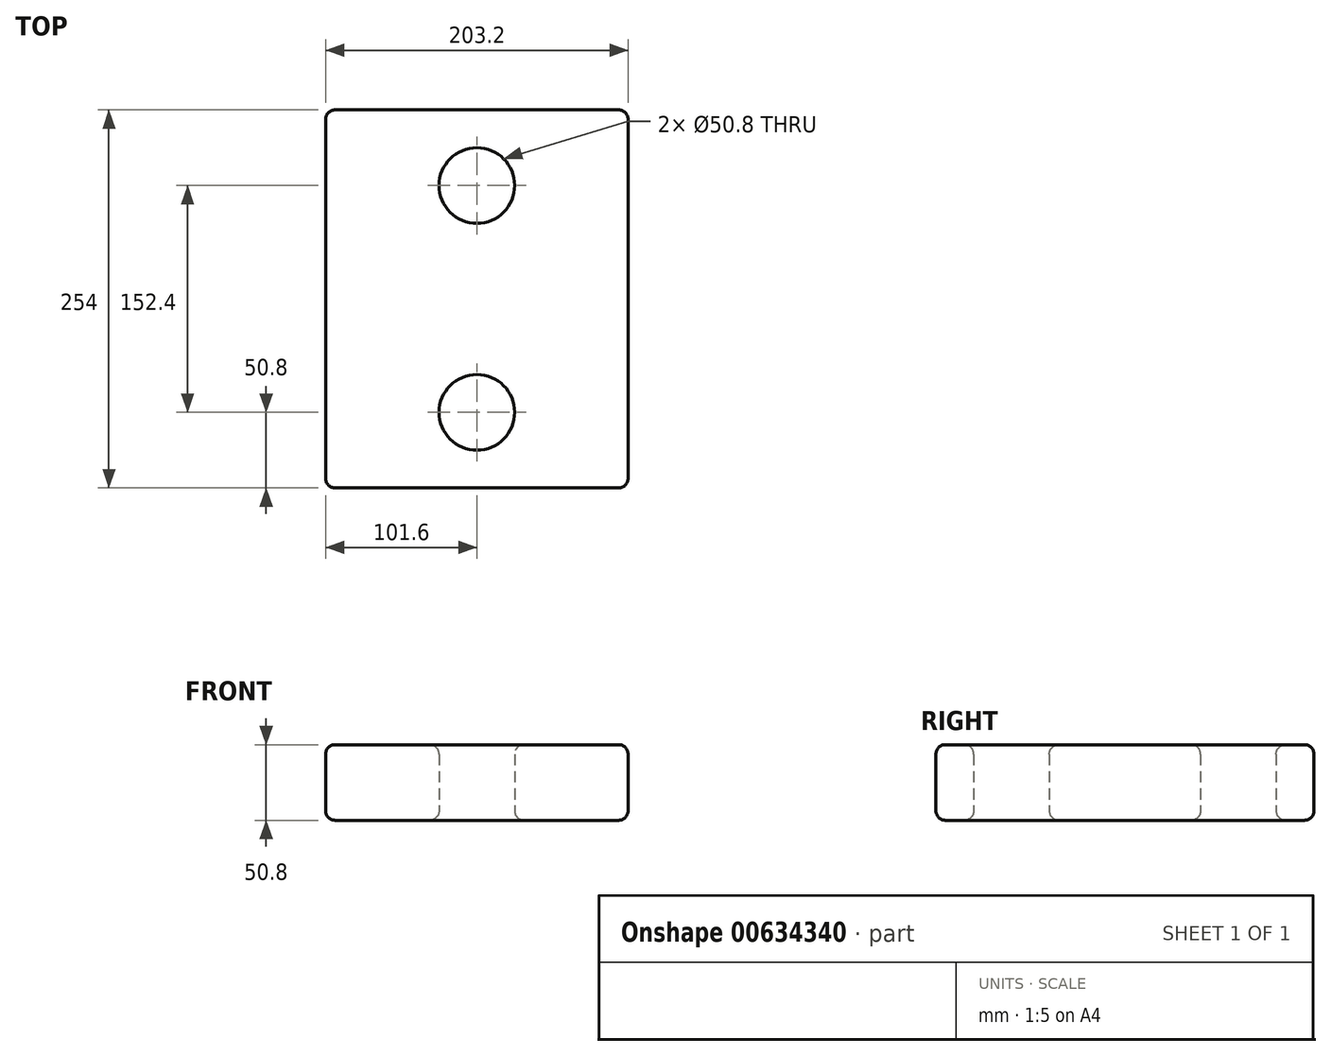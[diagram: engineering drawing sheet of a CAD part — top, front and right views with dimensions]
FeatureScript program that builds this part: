
annotation { "Feature Type Name" : "Feature", "Feature Type Description" : "" }
export const myFeature = defineFeature(function(context is Context, id is Id, definition is map)
    precondition{}
    {
        {
            var Q0;
            Q0=qCreatedBy(makeId("Top.planeOp"),FACE);
            var sketch = newSketch(context, id + "F0", { "sketchPlane" : qUnion([Q0])});
            skLineSegment(sketch, "E0.bottom", {"start": v(0, 0) * mm, "end": v(203.2, 0) * mm});
            skLineSegment(sketch, "E0.top", {"start": v(0, 254) * mm, "end": v(203.2, 254) * mm});
            skLineSegment(sketch, "E0.left", {"start": v(0, 0) * mm, "end": v(0, 254) * mm});
            skLineSegment(sketch, "E0.right", {"start": v(203.2, 0) * mm, "end": v(203.2, 254) * mm});
            skCircle(sketch, "E1", {"center": v(101.6, 203.2) * mm, "radius": 25.4 * mm});
            skPoint(sketch, "E1.centerSnap0", {"position": v(101.6, 254) * mm});
            skLineSegment(sketch, "E2", {"start": v(0, 127) * mm, "end": v(203.2, 127) * mm, "construction": true});
            skCircle(sketch, "E3.MirrorC", {"center": v(101.6, 50.8) * mm, "radius": 25.4 * mm});
            skSolve(sketch);
        }
        {
            var Q0;
            Q0=makeQuery(id+"F0.imprint","IMPRINT",FACE,{"disambiguationData":[TD([[makeQuery(id+"F0.imprint","IMPRINT",EDGE,{"derivedFrom":sQuery(id+"F0.wireOp",EDGE,"E0.bottom")}),1.0]])]});
            extrude(context, id + "F1", {"entities" : qUnion([Q0]), "depth" : 50.8 * mm, "offsetDistance" : 25.4 * mm});
        }
        {
            var Q0;
            Q0=makeQuery(id+"F1.opExtrude","CAP_EDGE",EDGE,{"disambiguationData":[OSD([sQuery(id+"F0.wireOp",EDGE,"E1")])],"isStart":false});
            var Q1;
            Q1=makeQuery(id+"F1.opExtrude","CAP_EDGE",EDGE,{"disambiguationData":[OSD([sQuery(id+"F0.wireOp",EDGE,"E3.MirrorC")])],"isStart":false});
            var Q2;
            Q2=makeQuery(id+"F1.opExtrude","CAP_EDGE",EDGE,{"disambiguationData":[OSD([sQuery(id+"F0.wireOp",EDGE,"E0.bottom")])],"isStart":false});
            var Q3;
            Q3=makeQuery(id+"F1.opExtrude","CAP_EDGE",EDGE,{"disambiguationData":[OSD([sQuery(id+"F0.wireOp",EDGE,"E0.right")])],"isStart":false});
            var Q4;
            Q4=makeQuery(id+"F1.opExtrude","CAP_EDGE",EDGE,{"disambiguationData":[OSD([sQuery(id+"F0.wireOp",EDGE,"E0.left")])],"isStart":false});
            var Q5;
            Q5=makeQuery(id+"F1.opExtrude","CAP_EDGE",EDGE,{"disambiguationData":[OSD([sQuery(id+"F0.wireOp",EDGE,"E0.left")])],"isStart":true});
            var Q6;
            Q6=makeQuery(id+"F1.opExtrude","SWEPT_EDGE",EDGE,{"disambiguationData":[OSD([sQuery(id+"F0.wireOp",EDGE,"E0.bottom"),sQuery(id+"F0.wireOp",EDGE,"E0.left")])]});
            var Q7;
            Q7=makeQuery(id+"F1.opExtrude","SWEPT_EDGE",EDGE,{"disambiguationData":[OSD([sQuery(id+"F0.wireOp",EDGE,"E0.top"),sQuery(id+"F0.wireOp",EDGE,"E0.left")])]});
            var Q8;
            Q8=makeQuery(id+"F1.opExtrude","CAP_EDGE",EDGE,{"disambiguationData":[OSD([sQuery(id+"F0.wireOp",EDGE,"E0.top")])],"isStart":false});
            var Q9;
            Q9=makeQuery(id+"F1.opExtrude","CAP_EDGE",EDGE,{"disambiguationData":[OSD([sQuery(id+"F0.wireOp",EDGE,"E0.top")])],"isStart":true});
            var Q10;
            Q10=makeQuery(id+"F1.opExtrude","SWEPT_EDGE",EDGE,{"disambiguationData":[OSD([sQuery(id+"F0.wireOp",EDGE,"E0.top"),sQuery(id+"F0.wireOp",EDGE,"E0.right")])]});
            var Q11;
            Q11=makeQuery(id+"F1.opExtrude","SWEPT_EDGE",EDGE,{"disambiguationData":[OSD([sQuery(id+"F0.wireOp",EDGE,"E0.bottom"),sQuery(id+"F0.wireOp",EDGE,"E0.right")])]});
            var Q12;
            Q12=makeQuery(id+"F1.opExtrude","CAP_EDGE",EDGE,{"disambiguationData":[OSD([sQuery(id+"F0.wireOp",EDGE,"E0.bottom")])],"isStart":true});
            var Q13;
            Q13=makeQuery(id+"F1.opExtrude","CAP_EDGE",EDGE,{"disambiguationData":[OSD([sQuery(id+"F0.wireOp",EDGE,"E0.right")])],"isStart":true});
            var Q14;
            Q14=makeQuery(id+"F1.opExtrude","CAP_EDGE",EDGE,{"disambiguationData":[OSD([sQuery(id+"F0.wireOp",EDGE,"E3.MirrorC")])],"isStart":true});
            var Q15;
            Q15=makeQuery(id+"F1.opExtrude","CAP_EDGE",EDGE,{"disambiguationData":[OSD([sQuery(id+"F0.wireOp",EDGE,"E1")])],"isStart":true});
            fillet(context, id + "F2", {"entities" : qUnion([Q0, Q1, Q2, Q3, Q4, Q5, Q6, Q7, Q8, Q9, Q10, Q11, Q12, Q13, Q14, Q15]), "radius" : 6.35 * mm, "tangentPropagation" : true, "allowEdgeOverflow" : false});
        }
    });
